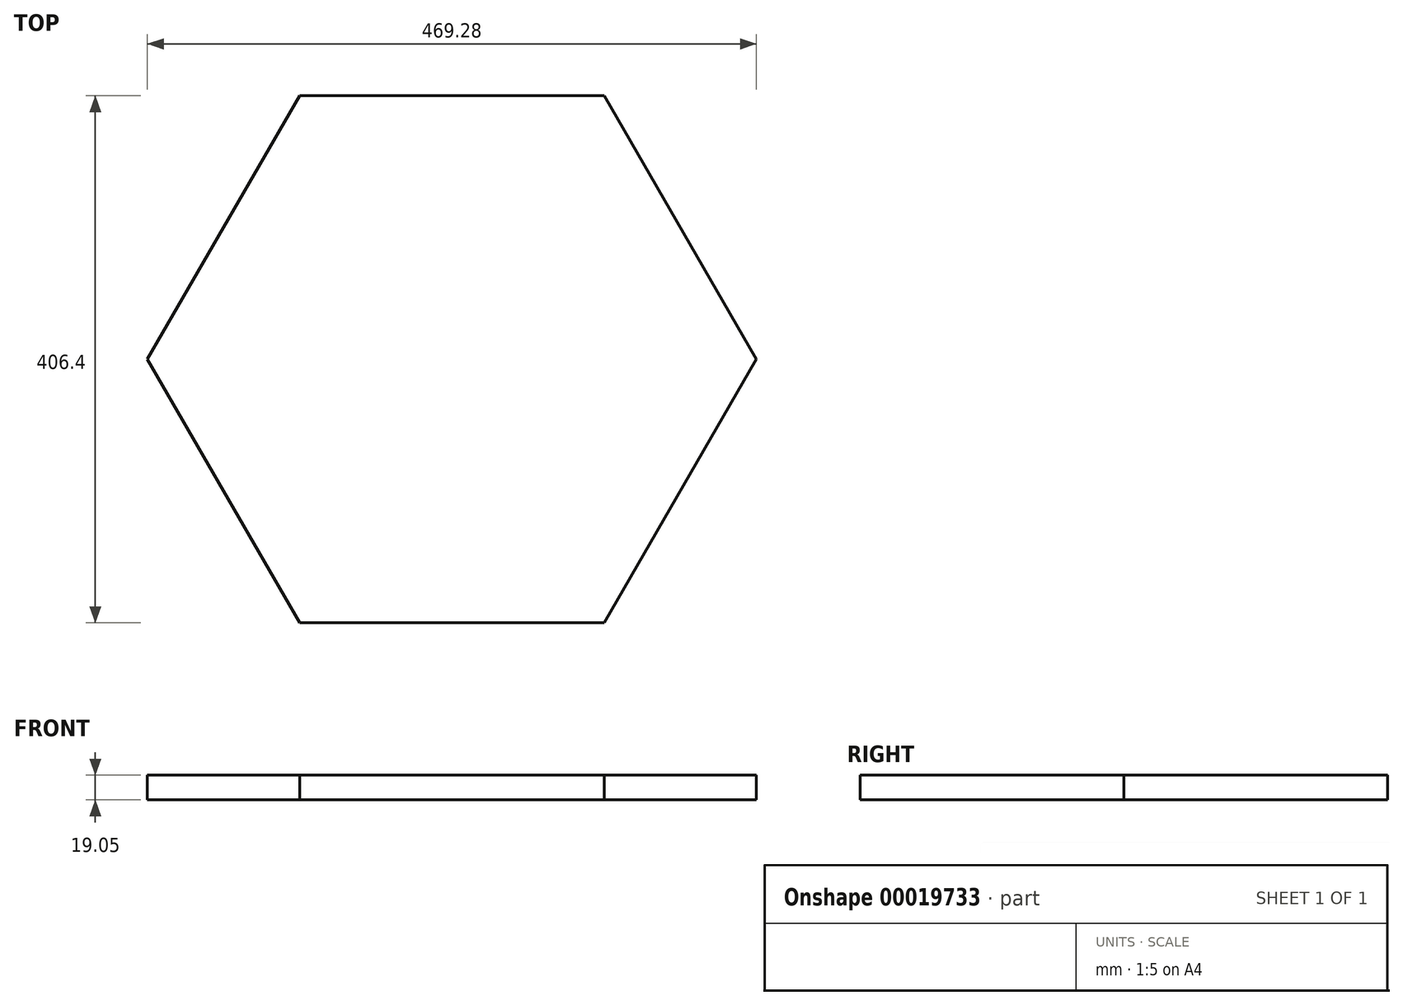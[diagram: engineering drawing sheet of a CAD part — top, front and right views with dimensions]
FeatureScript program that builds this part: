
annotation { "Feature Type Name" : "Feature", "Feature Type Description" : "" }
export const myFeature = defineFeature(function(context is Context, id is Id, definition is map)
    precondition{}
    {
        {
            var Q0;
            Q0=qCreatedBy(makeId("Top.planeOp"),FACE);
            var sketch = newSketch(context, id + "F0", { "sketchPlane" : qUnion([Q0])});
            skCircle(sketch, "E0.cCircle", {"center": v(0, 0) * mm, "radius": 234.64 * mm, "construction": true});
            skLineSegment(sketch, "E0.0", {"start": v(234.64, 0) * mm, "end": v(117.32, -203.2) * mm});
            skLineSegment(sketch, "E0.1", {"start": v(117.32, -203.2) * mm, "end": v(-117.32, -203.2) * mm});
            skLineSegment(sketch, "E0.2", {"start": v(-117.32, -203.2) * mm, "end": v(-234.64, 0) * mm});
            skLineSegment(sketch, "E0.3", {"start": v(-234.64, 0) * mm, "end": v(-117.32, 203.2) * mm});
            skLineSegment(sketch, "E0.4", {"start": v(-117.32, 203.2) * mm, "end": v(117.32, 203.2) * mm});
            skLineSegment(sketch, "E0.5", {"start": v(117.32, 203.2) * mm, "end": v(234.64, 0) * mm});
            skSolve(sketch);
        }
        {
            var Q0;
            Q0=makeQuery(id+"F0.imprint","IMPRINT",FACE,{"disambiguationData":[TD([[makeQuery(id+"F0.imprint","IMPRINT",EDGE,{"derivedFrom":sQuery(id+"F0.wireOp",EDGE,"E0.0")}),-1.0]])]});
            extrude(context, id + "F1", {"entities" : qUnion([Q0]), "depth" : 19.05 * mm});
        }
    });
